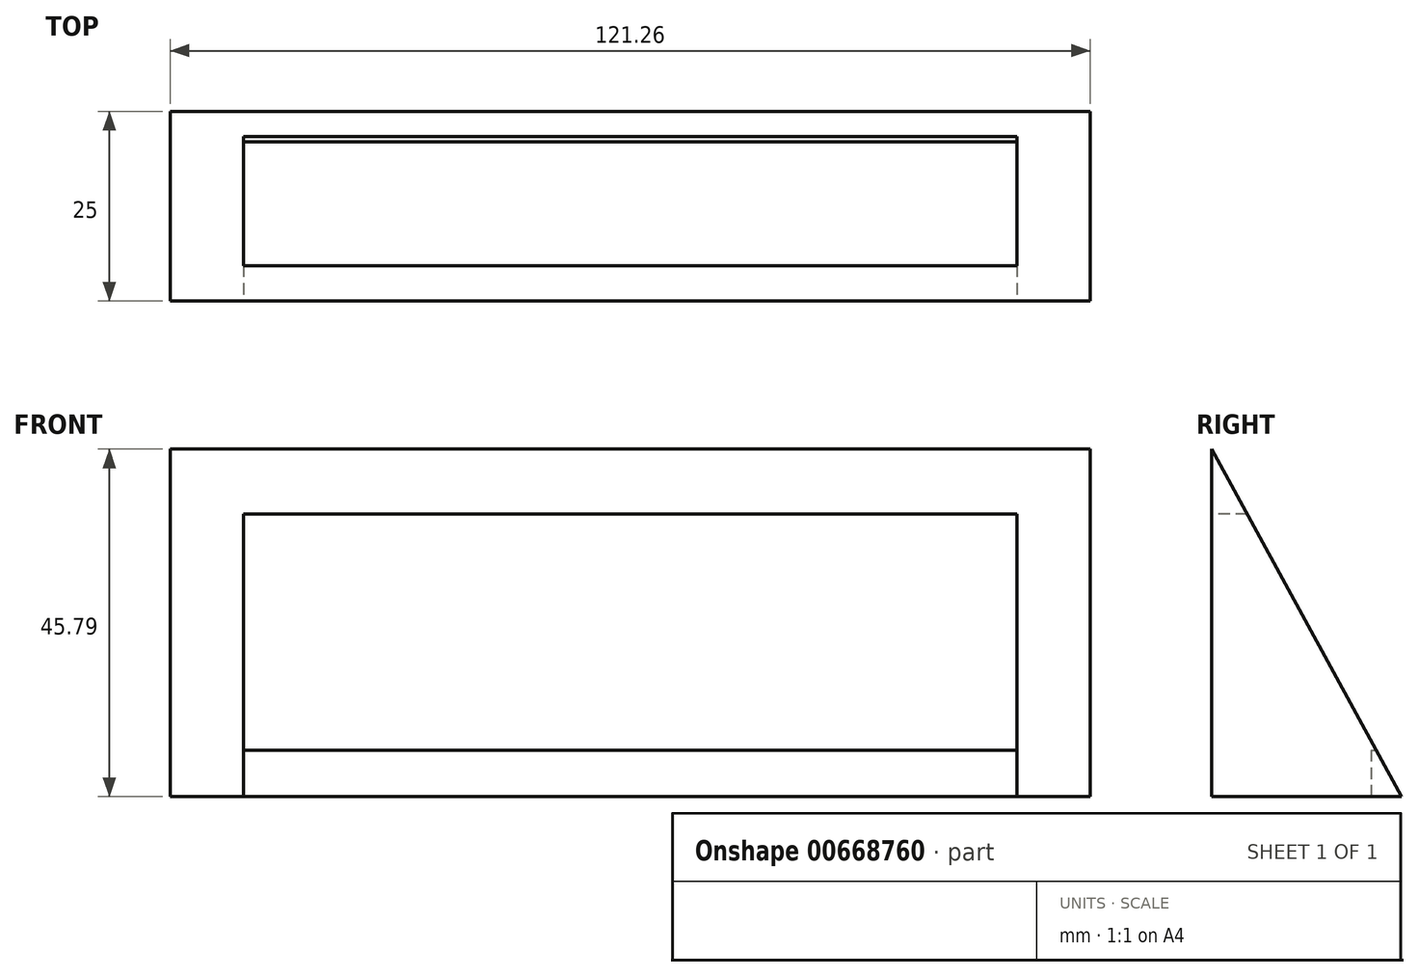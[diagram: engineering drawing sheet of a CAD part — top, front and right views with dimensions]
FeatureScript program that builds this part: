
annotation { "Feature Type Name" : "Feature", "Feature Type Description" : "" }
export const myFeature = defineFeature(function(context is Context, id is Id, definition is map)
    precondition{}
    {
        {
            var Q0;
            Q0=qCreatedBy(makeId("Front.planeOp"),FACE);
            var sketch = newSketch(context, id + "F0", { "sketchPlane" : qUnion([Q0])});
            skLineSegment(sketch, "E0", {"start": v(-62.63, 0) * mm, "end": v(-62.63, 45.8) * mm});
            skLineSegment(sketch, "E1", {"start": v(-62.63, 45.8) * mm, "end": v(58.63, 45.8) * mm});
            skLineSegment(sketch, "E2", {"start": v(58.63, 45.8) * mm, "end": v(58.63, 0) * mm});
            skLineSegment(sketch, "E3", {"start": v(58.63, 0) * mm, "end": v(48.93, 0) * mm});
            skLineSegment(sketch, "E4", {"start": v(48.93, 0) * mm, "end": v(48.93, 37.24) * mm});
            skLineSegment(sketch, "E5", {"start": v(48.93, 37.24) * mm, "end": v(-52.93, 37.24) * mm});
            skLineSegment(sketch, "E6", {"start": v(-52.93, 37.24) * mm, "end": v(-52.93, 0) * mm});
            skLineSegment(sketch, "E7", {"start": v(-52.93, 0) * mm, "end": v(-62.63, 0) * mm});
            skSolve(sketch);
        }
        {
            var Q0;
            Q0 = qSketchRegion(id + "F0", true);
            extrude(context, id + "F1", {"entities" : qUnion([Q0]), "oppositeDirection" : true, "depth" : 25 * mm, "offsetDistance" : 25 * mm});
        }
        {
            var Q0;
            Q0=makeQuery(id+"F1.opExtrude","CAP_FACE",FACE,{"disambiguationData":[OSD([sQuery(id+"F0.wireOp",EDGE,"E0"),sQuery(id+"F0.wireOp",EDGE,"E1"),sQuery(id+"F0.wireOp",EDGE,"E2"),sQuery(id+"F0.wireOp",EDGE,"E3"),sQuery(id+"F0.wireOp",EDGE,"E4"),sQuery(id+"F0.wireOp",EDGE,"E5"),sQuery(id+"F0.wireOp",EDGE,"E6"),sQuery(id+"F0.wireOp",EDGE,"E7")])],"isStart":false});
            var sketch = newSketch(context, id + "F2", { "sketchPlane" : qUnion([Q0])});
            skLineSegment(sketch, "E8", {"start": v(-48.93, 0) * mm, "end": v(52.93, 0) * mm});
            skLineSegment(sketch, "E9", {"start": v(52.93, 0) * mm, "end": v(52.93, 6.13) * mm});
            skLineSegment(sketch, "E10", {"start": v(52.93, 6.13) * mm, "end": v(-48.93, 6.13) * mm});
            skLineSegment(sketch, "E11", {"start": v(-48.93, 6.13) * mm, "end": v(-48.93, 0) * mm});
            skLineSegment(sketch, "E12", {"start": v(-48.93, 37.24) * mm, "end": v(52.93, 6.13) * mm});
            skLineSegment(sketch, "E13", {"start": v(-48.93, 6.13) * mm, "end": v(52.93, 37.24) * mm});
            skLineSegment(sketch, "E14", {"start": v(52.93, 37.24) * mm, "end": v(52.93, 6.13) * mm});
            skSolve(sketch);
        }
        {
            var Q0;
            Q0=makeQuery(id+"F2.imprint","IMPRINT",FACE,{"disambiguationData":[TD([[makeQuery(id+"F2.imprint","IMPRINT",EDGE,{"derivedFrom":sQuery(id+"F2.wireOp",EDGE,"E8")}),1.0]])]});
            extrude(context, id + "F3", {"entities" : qUnion([Q0]), "operationType" : NewBodyOperationType.ADD, "oppositeDirection" : true, "depth" : 4 * mm, "offsetDistance" : 25 * mm});
        }
        {
            var Q0;
            Q0=makeQuery(id+"F1.opExtrude","SWEPT_FACE",FACE,{"disambiguationData":[OSD([sQuery(id+"F0.wireOp",EDGE,"E0")])]});
            var sketch = newSketch(context, id + "F4", { "sketchPlane" : qUnion([Q0])});
            skLineSegment(sketch, "E15", {"start": v(0, 45.8) * mm, "end": v(-25, 0) * mm});
            skLineSegment(sketch, "E16", {"start": v(-25, 0) * mm, "end": v(-25, 45.8) * mm});
            skLineSegment(sketch, "E17", {"start": v(-25, 45.8) * mm, "end": v(0, 45.8) * mm});
            skSolve(sketch);
        }
        {
            var Q0;
            Q0=makeQuery(id+"F4.imprint","IMPRINT",FACE,{"disambiguationData":[TD([[makeQuery(id+"F4.imprint","IMPRINT",EDGE,{"derivedFrom":sQuery(id+"F4.wireOp",EDGE,"E15")}),-1.0]])]});
            extrude(context, id + "F5", {"entities" : qUnion([Q0]), "operationType" : NewBodyOperationType.REMOVE, "oppositeDirection" : true, "depth" : 500 * mm, "offsetDistance" : 25 * mm});
        }
    });
